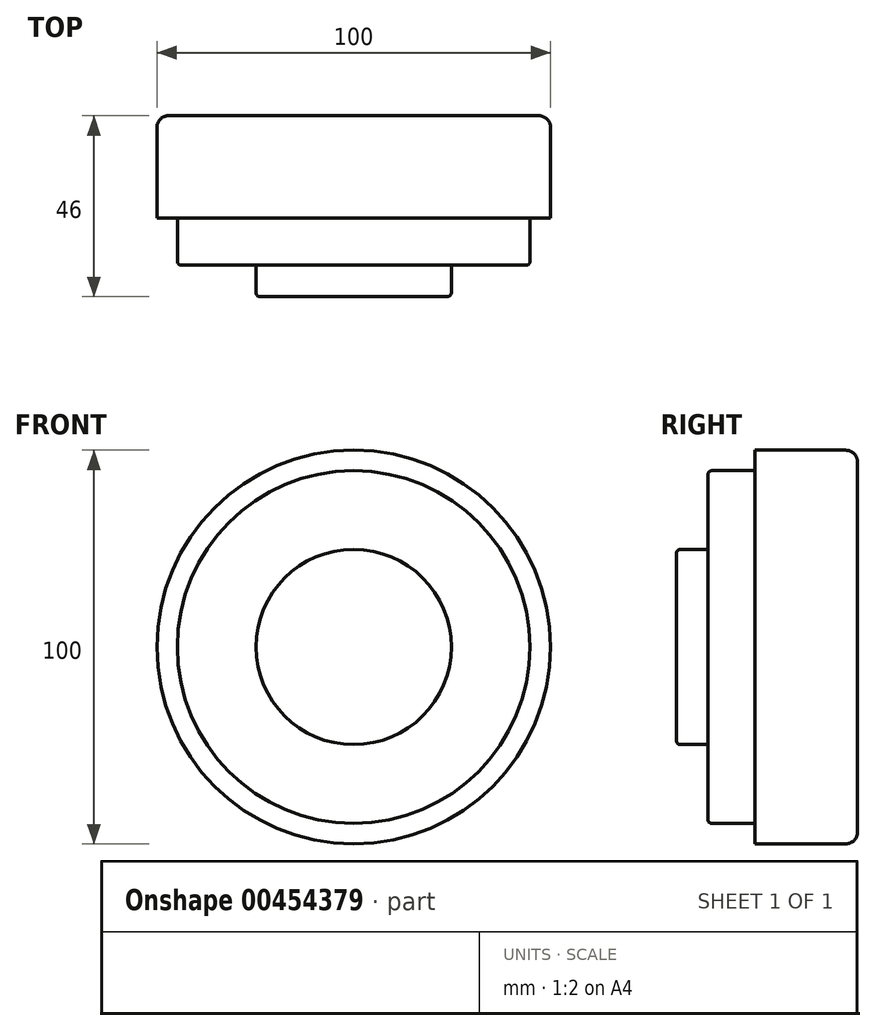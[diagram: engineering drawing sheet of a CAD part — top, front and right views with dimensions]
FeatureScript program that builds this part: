
annotation { "Feature Type Name" : "Feature", "Feature Type Description" : "" }
export const myFeature = defineFeature(function(context is Context, id is Id, definition is map)
    precondition{}
    {
        {
            var Q0;
            Q0=qCreatedBy(makeId("Right.planeOp"),FACE);
            var sketch = newSketch(context, id + "F0", { "sketchPlane" : qUnion([Q0])});
            skLineSegment(sketch, "E0", {"start": v(-20.82, 24.35) * mm, "end": v(25.18, 24.35) * mm});
            skLineSegment(sketch, "E1", {"start": v(25.18, 24.35) * mm, "end": v(25.18, 74.35) * mm});
            skLineSegment(sketch, "E2", {"start": v(25.18, 74.35) * mm, "end": v(-0.82, 74.35) * mm});
            skLineSegment(sketch, "E3", {"start": v(-0.82, 74.35) * mm, "end": v(-0.82, 69.15) * mm});
            skLineSegment(sketch, "E4", {"start": v(-0.82, 69.15) * mm, "end": v(-12.82, 69.15) * mm});
            skLineSegment(sketch, "E5", {"start": v(-12.82, 69.15) * mm, "end": v(-12.82, 49.15) * mm});
            skLineSegment(sketch, "E6", {"start": v(-12.82, 49.15) * mm, "end": v(-20.82, 49.15) * mm});
            skLineSegment(sketch, "E7", {"start": v(-20.82, 49.15) * mm, "end": v(-20.82, 24.35) * mm});
            skSolve(sketch);
        }
        {
            var Q0;
            Q0=makeQuery(id+"F0.imprint","IMPRINT",FACE,{"disambiguationData":[TD([[makeQuery(id+"F0.imprint","IMPRINT",EDGE,{"derivedFrom":sQuery(id+"F0.wireOp",EDGE,"E0")}),1.0]])]});
            var Q1;
            Q1=sQuery(id+"F0.wireOp",EDGE,"E0");
            revolve(context, id + "F1", {"entities" : qUnion([Q0]), "axis" : qUnion([Q1]), "revolveType" : RevolveType.FULL});
        }
        {
            var Q0;
            Q0=makeQuery(id+"F1.opRevolve","SWEPT_EDGE",EDGE,{"disambiguationData":[OSD([sQuery(id+"F0.wireOp",EDGE,"E1"),sQuery(id+"F0.wireOp",EDGE,"E2")])]});
            fillet(context, id + "F2", {"entities" : qUnion([Q0]), "radius" : 3 * mm, "tangentPropagation" : true, "allowEdgeOverflow" : false});
        }
        {
            var Q0;
            Q0=makeQuery(id+"F1.opRevolve","SWEPT_EDGE",EDGE,{"disambiguationData":[OSD([sQuery(id+"F0.wireOp",EDGE,"E4"),sQuery(id+"F0.wireOp",EDGE,"E5")])]});
            fillet(context, id + "F3", {"entities" : qUnion([Q0]), "radius" : 1 * mm, "tangentPropagation" : true, "allowEdgeOverflow" : false});
        }
        {
            var Q0;
            Q0=makeQuery(id+"F1.opRevolve","SWEPT_EDGE",EDGE,{"disambiguationData":[OSD([sQuery(id+"F0.wireOp",EDGE,"E6"),sQuery(id+"F0.wireOp",EDGE,"E7")])]});
            fillet(context, id + "F4", {"entities" : qUnion([Q0]), "radius" : 1 * mm, "tangentPropagation" : true, "allowEdgeOverflow" : false});
        }
    });
